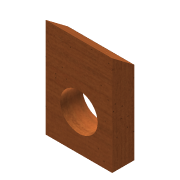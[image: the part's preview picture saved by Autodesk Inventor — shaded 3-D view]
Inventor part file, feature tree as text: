
AUTODESK INVENTOR PART (.ipt)
format: ipt  version: 2016 SP2 (Build 200236200, 236)  size: 114,688 bytes
history: native  units: in
note: dims shown in document units (in); Inventor stores cm internally (conversion verified against a paired STEP export)
features: sketch x3, hole x2, extrude x1
ambient origin geometry x8: Origin, YZ Plane, XZ Plane, XY Plane, X Axis, Y Axis, Z Axis, Center Point
bodies: Solid1 (feature_tree)
feature tree (6):
  extrude  "Extrusion1"  Depth=1.4961in
  hole  "Hole2"  [1 undecoded]
  hole  "Hole3"  [1 undecoded]
  sketch  "Sketch1"  dims[d2=6.6929in d4=1.4961in]
  sketch  "Sketch4"  dims[d6=4.4882in d7=0.0in d26=0.8727in]
  sketch  "Sketch5"  dims[d28=0.7874in d30=2.2441in d31=0.3937in d33=1.0in d35=0.0394in d36=0.75in d37=0.375in d38=0.25in d39=0.5635in d40=1.0in d41=0.8108in d42=1.122in d44=2.5197in d45=4.252in d46=2.5197in d47=0.2362in d48=0.1575in d49=0.0787in d50=90.0deg d51=0.315in d52=0.8108in]
note: 2 required parameter values undecoded (feature->parameter linkage not recoverable at this tier; creation-order binding heuristic only, values carry confidence <= 0.55)
